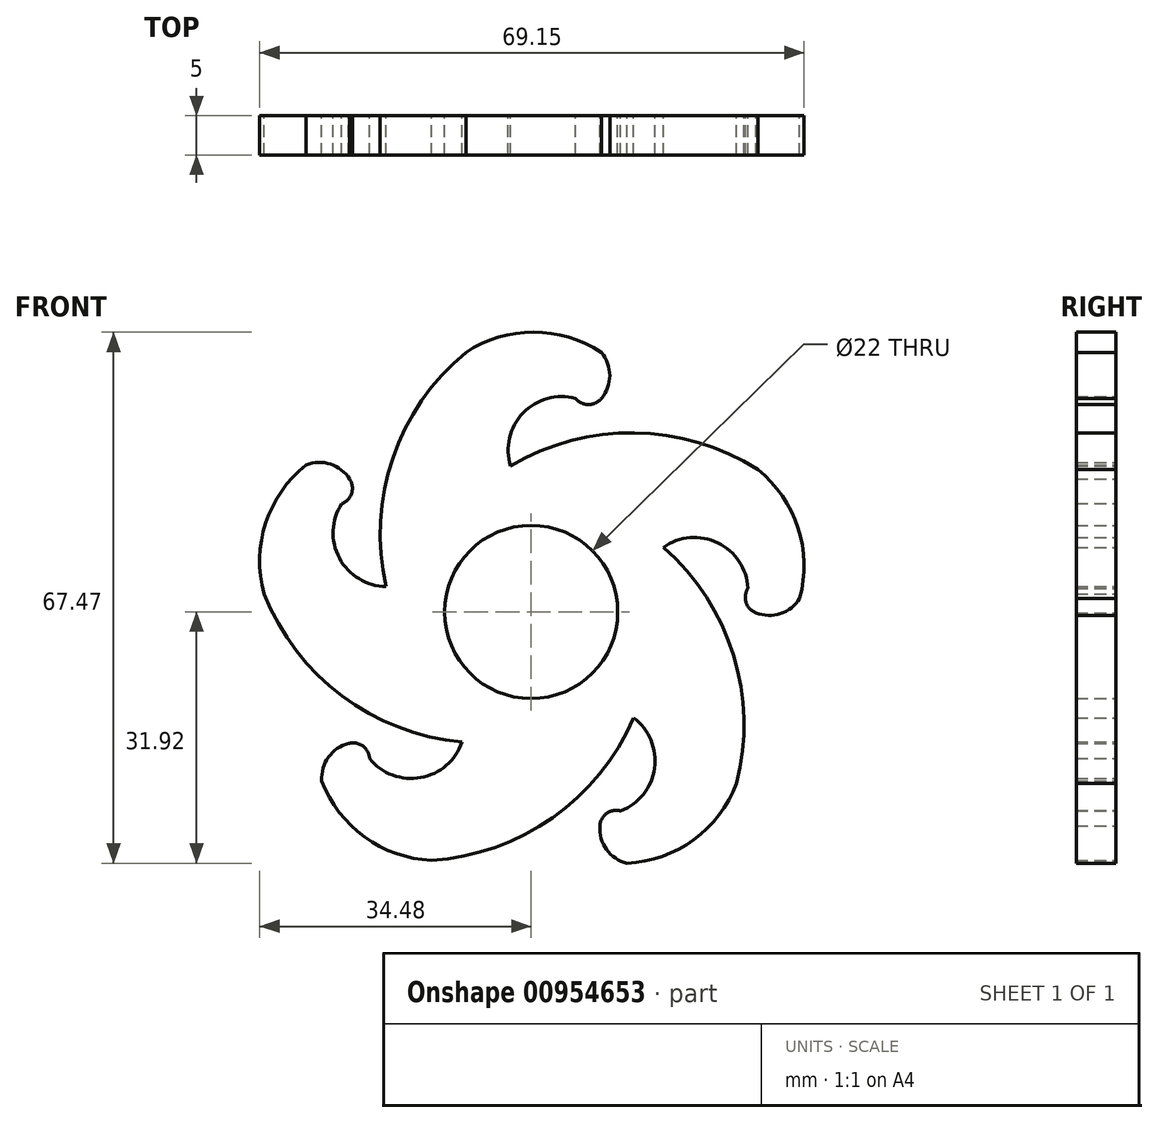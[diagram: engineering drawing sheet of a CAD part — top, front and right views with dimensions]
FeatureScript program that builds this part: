
annotation { "Feature Type Name" : "Feature", "Feature Type Description" : "" }
export const myFeature = defineFeature(function(context is Context, id is Id, definition is map)
    precondition{}
    {
        {
            var Q0;
            Q0=qCreatedBy(makeId("Front.planeOp"),FACE);
            var sketch = newSketch(context, id + "F0", { "sketchPlane" : qUnion([Q0])});
            skCircle(sketch, "E0", {"center": v(0, 0) * mm, "radius": 11 * mm});
            skCircle(sketch, "E1", {"center": v(0, 0) * mm, "radius": 17.5 * mm});
            skArc(sketch, "E2", {"start": v(-8.3, 32.97) * mm, "mid": v(-18.07, 17.93) * mm, "end": v(-17.5, 0) * mm});
            skArc(sketch, "E3", {"start": v(5.65, 27.13) * mm, "mid": v(7.28, 26.34) * mm, "end": v(8.92, 27.13) * mm});
            skArc(sketch, "E4", {"start": v(5.65, 27.13) * mm, "mid": v(-1.44, 24.8) * mm, "end": v(-2.14, 17.37) * mm});
            skArc(sketch, "E5", {"start": v(8.92, 32.97) * mm, "mid": v(0.3, 35.55) * mm, "end": v(-8.3, 32.97) * mm});
            skArc(sketch, "E6", {"start": v(8.92, 27.13) * mm, "mid": v(9.99, 30.05) * mm, "end": v(8.92, 32.97) * mm});
            skSolve(sketch);
        }
        {
            var Q0;
            Q0=makeQuery(id+"F0.imprint","IMPRINT",FACE,{"disambiguationData":[TD([[makeQuery(id+"F0.imprint","IMPRINT",EDGE,{"derivedFrom":sQuery(id+"F0.wireOp",EDGE,"E0")}),-1.0]])]});
            var Q1;
            {var subQ0=sQuery(id+"F0.wireOp",EDGE,"E2");Q1=makeQuery(id+"F0.imprint","IMPRINT",FACE,{"disambiguationData":[TD([[makeQuery(id+"F0.imprint","IMPRINT",EDGE,{"derivedFrom":subQ0}),1.0]])]});}
            extrude(context, id + "F1", {"entities" : qUnion([Q0, Q1]), "depth" : 5 * mm, "offsetDistance" : 25 * mm});
        }
        {
            var Q0;
            Q0=makeQuery(id+"F1.opExtrude","SWEPT_BODY",BODY,{"disambiguationData":[OSD([sQuery(id+"F0.wireOp",EDGE,"E0"),sQuery(id+"F0.wireOp",EDGE,"E1"),sQuery(id+"F0.wireOp",EDGE,"E2"),sQuery(id+"F0.wireOp",EDGE,"Ut1horLQ-he1D-MHaD-roNH-ywuWsNPrfH3A"),sQuery(id+"F0.wireOp",EDGE,"zYDmEe6e-Vxnr-qjGq-XeMf-bEcsOdEzqtx1"),sQuery(id+"F0.wireOp",EDGE,"E3"),sQuery(id+"F0.wireOp",EDGE,"E4")])]});
            var Q1;
            Q1=makeQuery(id+"F1.opExtrude","CAP_EDGE",EDGE,{"disambiguationData":[OSD([sQuery(id+"F0.wireOp",EDGE,"E0")])],"isStart":false});
            circularPattern(context, id + "F2", {"operationType" : NewBodyOperationType.ADD, "entities" : qUnion([Q0]), "axis" : qUnion([Q1]), "angle" : 360 * degree, "instanceCount" : 5, "equalSpace" : true});
        }
    });
